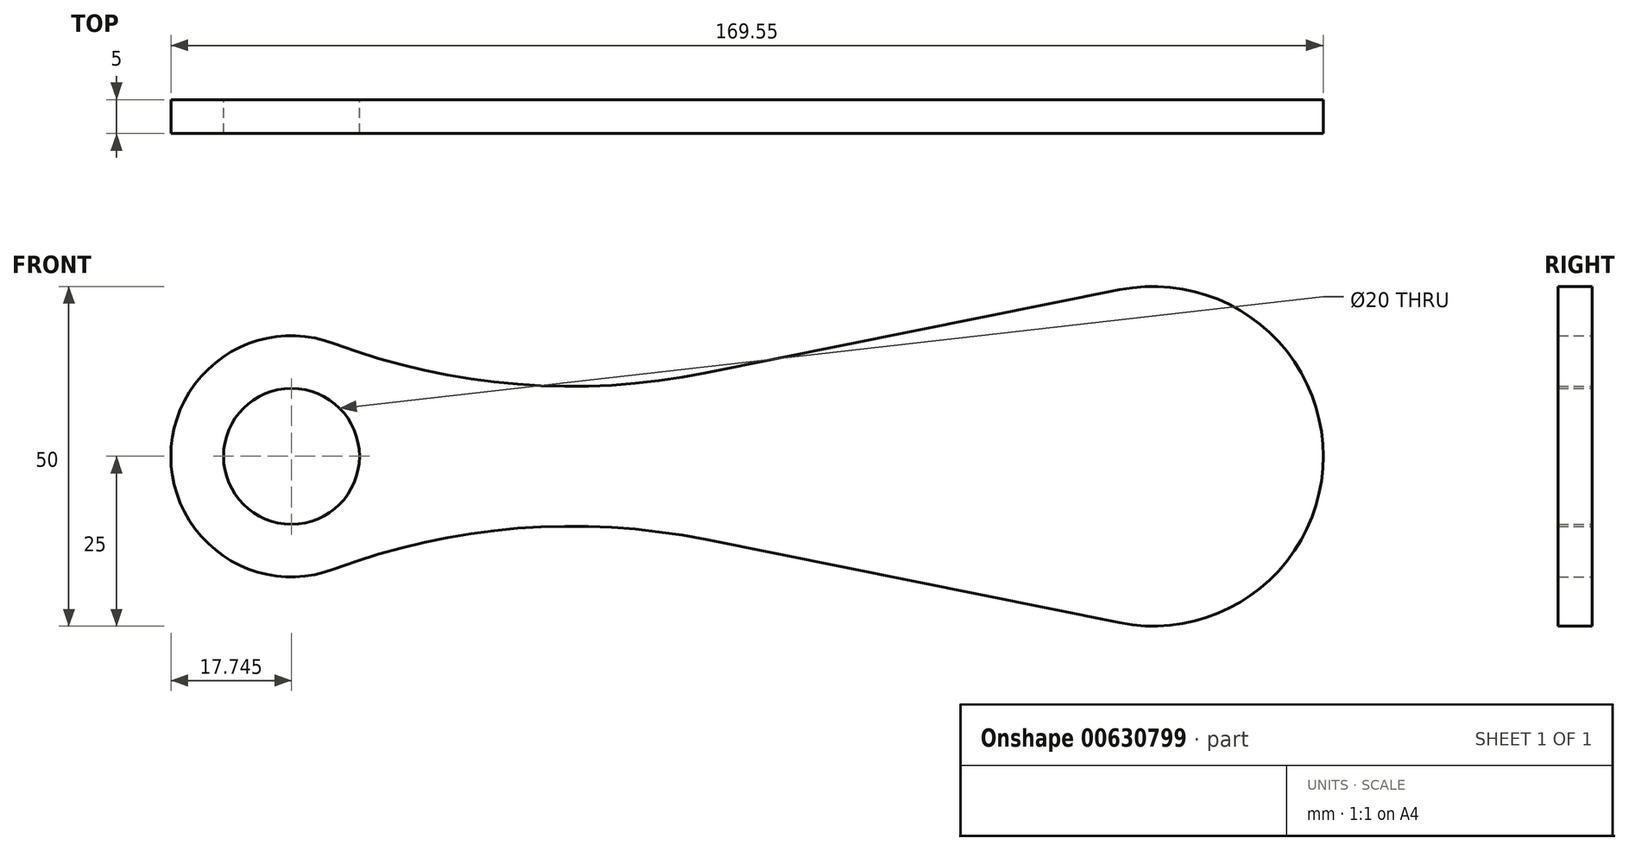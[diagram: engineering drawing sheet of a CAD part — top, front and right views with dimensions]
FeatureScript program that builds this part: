
annotation { "Feature Type Name" : "Feature", "Feature Type Description" : "" }
export const myFeature = defineFeature(function(context is Context, id is Id, definition is map)
    precondition{}
    {
        {
            var Q0;
            Q0=qCreatedBy(makeId("Front.planeOp"),FACE);
            var sketch = newSketch(context, id + "F0", { "sketchPlane" : qUnion([Q0])});
            skArc(sketch, "E0", {"start": v(20.07, -24.5) * mm, "mid": v(50, 0) * mm, "end": v(20.07, 24.5) * mm});
            skCircle(sketch, "E1", {"center": v(-101.8, 0) * mm, "radius": 10 * mm});
            skArc(sketch, "E2.0", {"start": v(-95.6, 16.62) * mm, "mid": v(-119.55, 0) * mm, "end": v(-95.6, -16.62) * mm});
            skLineSegment(sketch, "E3", {"start": v(-40.87, 12.25) * mm, "end": v(20.07, 24.5) * mm});
            skLineSegment(sketch, "E4", {"start": v(-40.87, -12.25) * mm, "end": v(20.07, -24.5) * mm});
            skPoint(sketch, "E5.visualSharp", {"position": v(-84.41, 3.5) * mm});
            skArc(sketch, "E5.filletArc", {"start": v(-95.6, 16.62) * mm, "mid": v(-68.54, 10.6) * mm, "end": v(-40.87, 12.25) * mm});
            skPoint(sketch, "E6.visualSharp", {"position": v(-84.41, -3.5) * mm});
            skArc(sketch, "E6.filletArc", {"start": v(-40.87, -12.25) * mm, "mid": v(-68.54, -10.6) * mm, "end": v(-95.6, -16.62) * mm});
            skSolve(sketch);
        }
        {
            var Q0;
            Q0=makeQuery(id+"F0.imprint","IMPRINT",FACE,{"disambiguationData":[TD([[makeQuery(id+"F0.imprint","IMPRINT",EDGE,{"derivedFrom":sQuery(id+"F0.wireOp",EDGE,"E0")}),1.0]])]});
            extrude(context, id + "F1", {"entities" : qUnion([Q0]), "depth" : 5 * mm, "offsetDistance" : 25 * mm});
        }
    });
